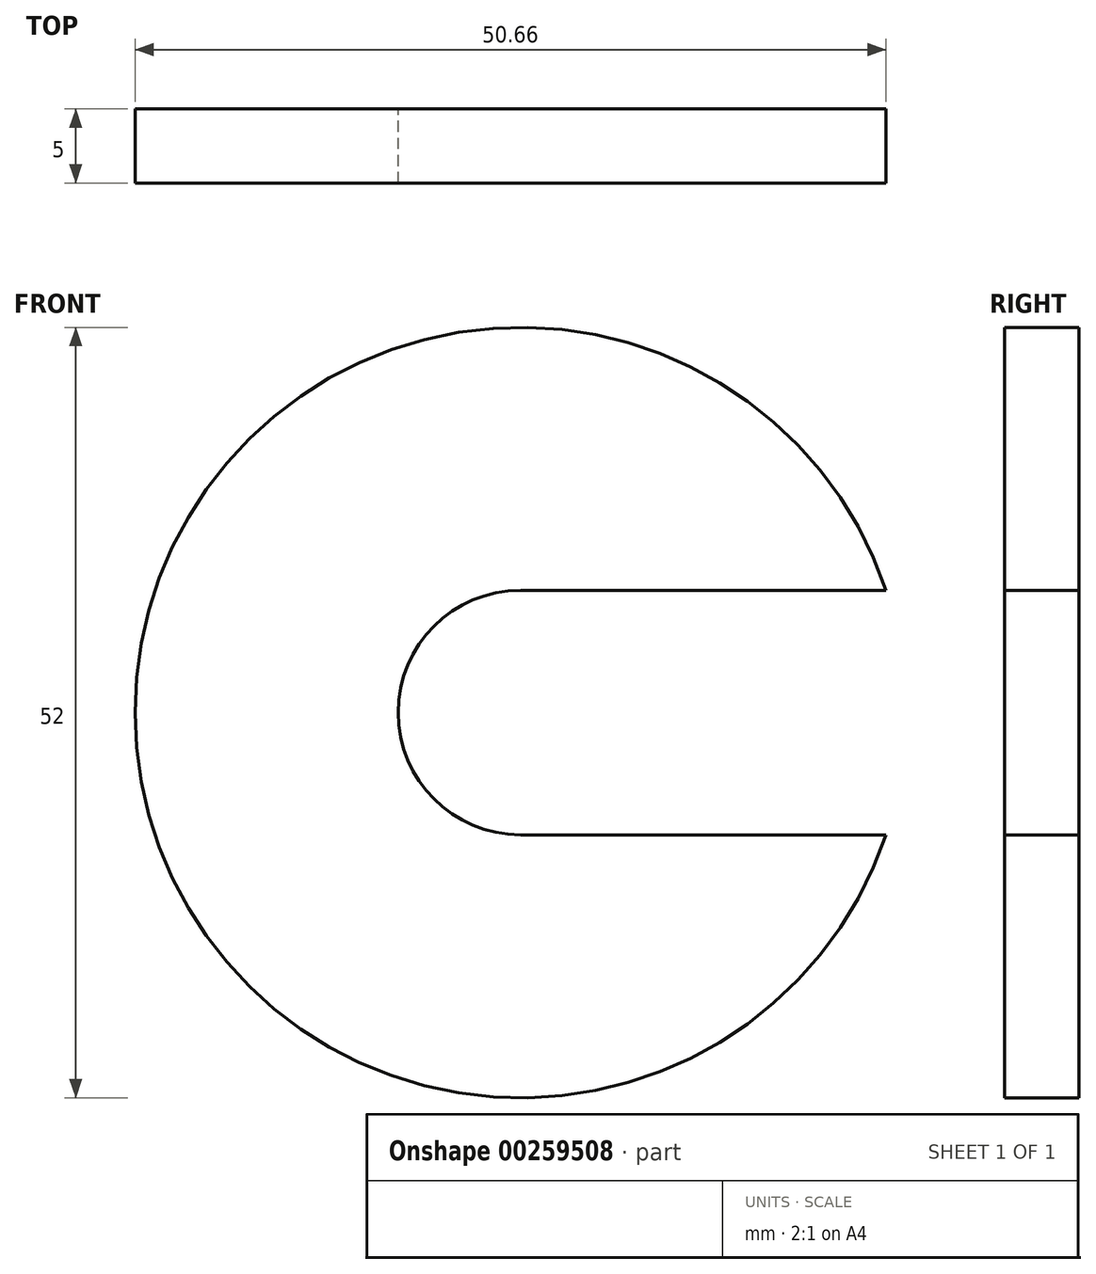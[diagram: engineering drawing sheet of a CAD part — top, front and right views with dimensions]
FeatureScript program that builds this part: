
annotation { "Feature Type Name" : "Feature", "Feature Type Description" : "" }
export const myFeature = defineFeature(function(context is Context, id is Id, definition is map)
    precondition{}
    {
        {
            var Q0;
            Q0=qCreatedBy(makeId("Front.planeOp"),FACE);
            var sketch = newSketch(context, id + "F0", { "sketchPlane" : qUnion([Q0])});
            skLineSegment(sketch, "E0", {"start": v(0, 8.25) * mm, "end": v(24.66, 8.25) * mm});
            skLineSegment(sketch, "E1", {"start": v(0, -8.25) * mm, "end": v(24.66, -8.25) * mm});
            skArc(sketch, "E2", {"start": v(0, 8.25) * mm, "mid": v(-8.25, 0) * mm, "end": v(0, -8.25) * mm});
            skArc(sketch, "E3", {"start": v(24.66, 8.25) * mm, "mid": v(-26, 0) * mm, "end": v(24.66, -8.25) * mm});
            skSolve(sketch);
        }
        {
            var Q0;
            Q0 = qSketchRegion(id + "F0", true);
            extrude(context, id + "F1", {"entities" : qUnion([Q0]), "depth" : 5 * mm});
        }
    });
